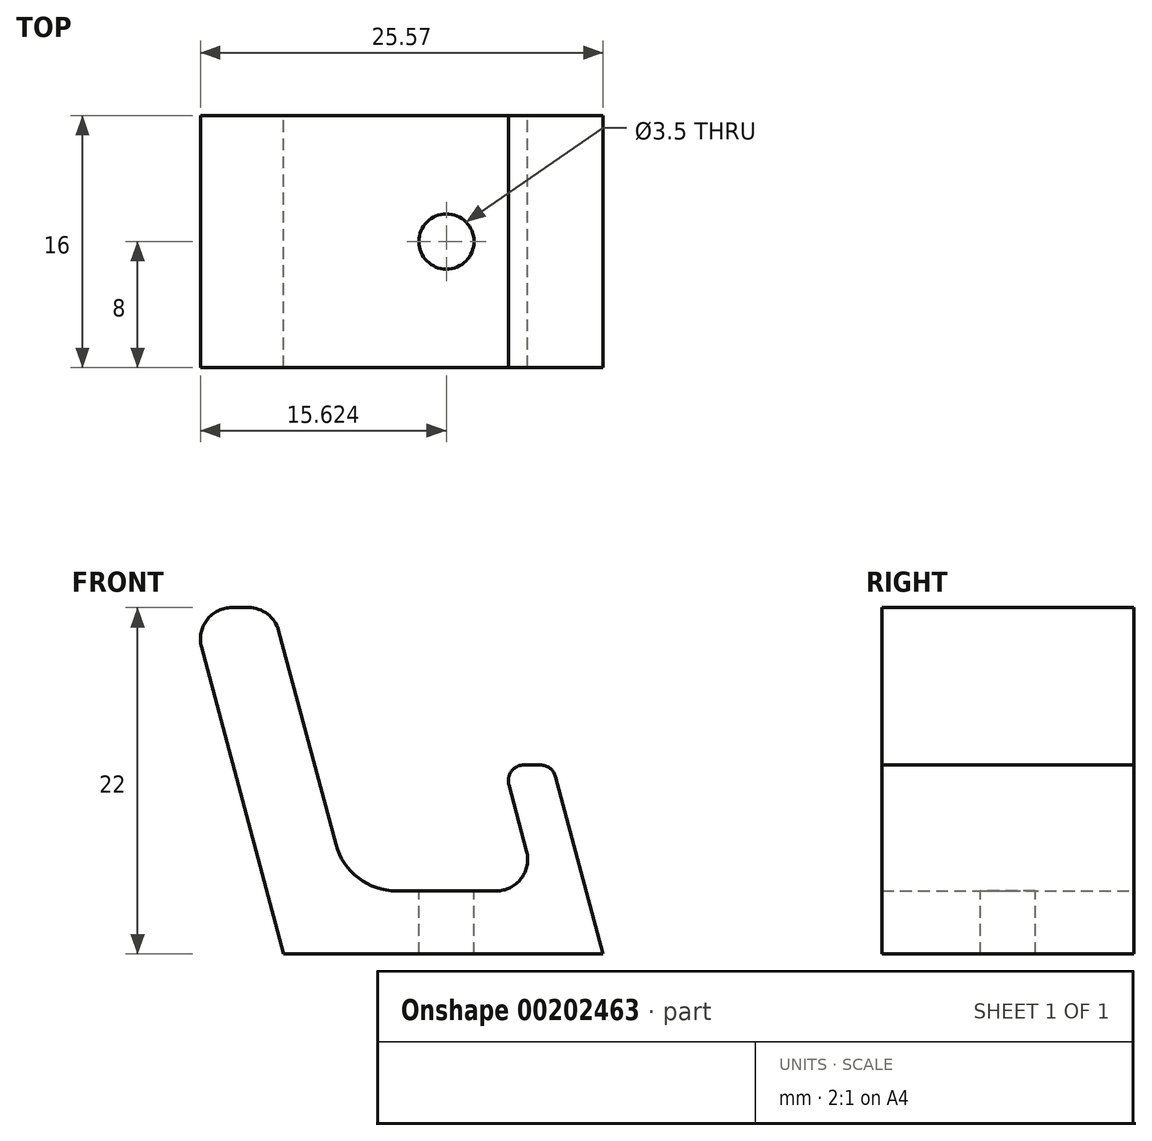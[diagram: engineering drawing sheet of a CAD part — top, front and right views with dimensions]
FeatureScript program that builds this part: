
annotation { "Feature Type Name" : "Feature", "Feature Type Description" : "" }
export const myFeature = defineFeature(function(context is Context, id is Id, definition is map)
    precondition{}
    {
        {
            var Q0;
            Q0=qCreatedBy(makeId("Front.planeOp"),FACE);
            var sketch = newSketch(context, id + "F0", { "sketchPlane" : qUnion([Q0])});
            skLineSegment(sketch, "E0", {"start": v(0, 0) * mm, "end": v(-20.28, 0) * mm});
            skLineSegment(sketch, "E1", {"start": v(-20.28, 0) * mm, "end": v(-25.5, 19.48) * mm});
            skLineSegment(sketch, "E2", {"start": v(-23.57, 22) * mm, "end": v(-22.54, 22) * mm});
            skLineSegment(sketch, "E3", {"start": v(-20.6, 20.52) * mm, "end": v(-16.97, 6.96) * mm});
            skLineSegment(sketch, "E4", {"start": v(-13.1, 4) * mm, "end": v(-6.78, 4) * mm});
            skLineSegment(sketch, "E5", {"start": v(-4.85, 6.52) * mm, "end": v(-5.98, 10.74) * mm});
            skLineSegment(sketch, "E6", {"start": v(-5.02, 12) * mm, "end": v(-3.98, 12) * mm});
            skLineSegment(sketch, "E7", {"start": v(-3.02, 11.26) * mm, "end": v(0, 0) * mm});
            skPoint(sketch, "E8.visualSharp", {"position": v(-16.18, 4) * mm});
            skArc(sketch, "E8.filletArc", {"start": v(-16.97, 6.96) * mm, "mid": v(-15.54, 4.83) * mm, "end": v(-13.1, 4) * mm});
            skPoint(sketch, "E9.visualSharp", {"position": v(-21, 22) * mm});
            skArc(sketch, "E9.filletArc", {"start": v(-20.6, 20.52) * mm, "mid": v(-21.32, 21.59) * mm, "end": v(-22.54, 22) * mm});
            skPoint(sketch, "E10.visualSharp", {"position": v(-26.18, 22) * mm});
            skArc(sketch, "E10.filletArc", {"start": v(-23.57, 22) * mm, "mid": v(-25.16, 21.22) * mm, "end": v(-25.5, 19.48) * mm});
            skPoint(sketch, "E11.visualSharp", {"position": v(-4.18, 4) * mm});
            skArc(sketch, "E11.filletArc", {"start": v(-6.78, 4) * mm, "mid": v(-5.2, 4.78) * mm, "end": v(-4.85, 6.52) * mm});
            skPoint(sketch, "E12.visualSharp", {"position": v(-6.32, 12) * mm});
            skArc(sketch, "E12.filletArc", {"start": v(-5.02, 12) * mm, "mid": v(-5.81, 11.6) * mm, "end": v(-5.98, 10.74) * mm});
            skPoint(sketch, "E13.visualSharp", {"position": v(-3.22, 12) * mm});
            skArc(sketch, "E13.filletArc", {"start": v(-3.02, 11.26) * mm, "mid": v(-3.37, 11.8) * mm, "end": v(-3.98, 12) * mm});
            skSolve(sketch);
        }
        {
            var Q0;
            Q0=qSketchRegion(id+"F0",true);
            extrude(context, id + "F1", {"entities" : qUnion([Q0]), "depth" : 8 * mm, "hasSecondDirection" : true, "secondDirectionOppositeDirection" : true, "secondDirectionDepth" : 8 * mm});
        }
        {
            var Q0;
            Q0=makeQuery(id+"F1.opExtrude","SWEPT_FACE",FACE,{"disambiguationData":[OSD([sQuery(id+"F0.wireOp",EDGE,"E4")])]});
            var sketch = newSketch(context, id + "F2", { "sketchPlane" : qUnion([Q0])});
            skCircle(sketch, "E14", {"center": v(-9.95, 0) * mm, "radius": 1.75 * mm});
            skLineSegment(sketch, "E15", {"start": v(-13.1, 0) * mm, "end": v(-6.78, 0) * mm, "construction": true});
            skSolve(sketch);
        }
        {
            var Q0;
            Q0=qSketchRegion(id+"F2",true);
            extrude(context, id + "F3", {"entities" : qUnion([Q0]), "operationType" : NewBodyOperationType.REMOVE, "endBound" : BoundingType.UP_TO_NEXT, "oppositeDirection" : true, "depth" : 25 * mm});
        }
    });
